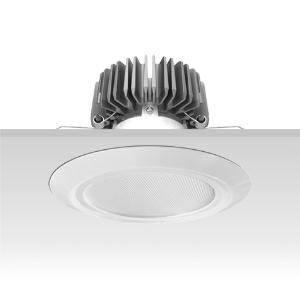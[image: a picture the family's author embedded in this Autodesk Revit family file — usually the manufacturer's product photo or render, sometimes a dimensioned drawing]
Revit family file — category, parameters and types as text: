
# Revit family: 3f_filippi_-_3f_reno_bianco_ampio_3f_filippi_-_30671_a01048_-_3f_reno_200_wh_2000-840_dali_wide___smp_wh_ad90
name_source: partatom
category: Lighting Fixtures
units: mm (PartAtom-declared; Revit-internal decimal feet)

## family parameters
Cut with Voids When Loaded = No
Host = Face
Light Source = No
Part Type = Normal
Room Calculation Point = No
Round Connector Dimension = Use Diameter
Shared = No

## types (1)
- 3F Filippi - 3F Reno Bianco Ampio (1 x LED, 1723 lm, 20 W, 4000 K)
    Apparent Load = 20 VA
    Approval mark = CE
    CIE Flux Codes = 74 92 98 100 100
    Color Rendering = 80
    Color Temperature = 4000 K
    Control Gear = Electronic transformer
    Default Elevation = 1800 mm
    Description = ILLUMINOTECHNICAL
Luminous efficiency 100% (DLOR 100%, ULOR 0%).
Initial luminous flux of the luminaire 1723 lm.
Direct symmetric wide distribution.
Installation Interdistance Transv.D = 1.06 x hu - Long.D = 1.04 x hu.
Average luminance <3000 cd/m² for radial angles >65°.
Tabular UGR (CIE 117 - 4H-8H; S=0.25H; 70/50/20): RUG 21.4 - 21.3.
Beam angle: 70° - 69°.
Luminous efficacy 86 lm/W.
Lifetime (L90/B10): 30000 h. (tq+25°C)
Lifetime (L85/B10): 50000 h. (tq+25°C)
Lifetime (L70/B10): 80000 h. (tq+25°C)
Sudden decreased luminous flux after 50000 hours: 0% (C0).
Photobiological safety in compliance with IEC/TR 62778: RG0 risk exempt, (IEC 62471).
In compliance with IEC/EN 62722-2-1 - IEC/EN 62717 standards.

SOURCE
Compact LED module 2000/840.
Energy efficiency class (UE 2019/2020 - UE 2019/2015): D.
CIE 13.3 Colour rendering index: CRI >80 (R9 <50%).
IES TM-30 Fidelity Index: Rf = 84 Rg = 95.
CCT nominal colour temperature 4000 K.
Colour initial tolerance (MacAdam): SDCM 3.
Zhaga Book 3 compliant.

MECHANICAL
Passive heat dissipator in die-casting aluminium, oversized, for optimum thermal management of the LED module.
Parabolic element with graduated/concentric rings in white polycarbonate.
Transparent external lens with glossy and satin differentiated surfaces, with a cooling and anti-insect system in methacrylate (PMMA).
Fastening spring clips in stainless steel.
Dimensions: diameter 226 mm, height 146 mm. Weight 1.1 kg.
IP44 protection degree for exposed part, IP20 for recessed part.
Mechanical strength to impacts IK05 (0.7 joule).
Glow-wire test resistance 650°C.

ELECTRICAL
Wiring on a separate unit.
Halogen Free DALI-2 DATI (Parts 251, 252, 253), PUSH-DIM, electronic wiring 230V-50/60Hz, power factor 0.90 at full load, THD <25%, constant output current, SELV, class II, 1 driver, 1 DALI addresse.
Power of the luminaire 20 W.
ENEC - CE.
SAFE FLICKER: PstLM=<1 and SVM=<0.4 (IEC TR 61547-1 and IEC TR 63158), to ensure a more comfortable and safe light.
Luminaire compliant with EN 60598-2-22 for power supply from a centralised emergency system CPSS (Central Power Supply System), not incorporated in the luminaire - high risk areas excluded. The default power and flux are 100% in AC and 100% in DC.
Ambient temperature from 0°C to +25°C.
Temperature class T6 max 85°C.
Relative humidity UR: <85%.

INSTALLATION
Pull-up recessed fitting.
False ceiling carving: 200 mm.
All accessories dedicated to this product are available on the Catalog and on our website www.3F-Filippi.com.

ACCESSORIES
A01048 - Anti-glare microprismatic SMP diffuser in methacrylate (PMMA), locked and in line with the trim, in white polycarbonate.

APPLICATIONS
Suitable product for food production plants (HACCP), IFS (Food Version 6), BRC (GSFS Food Version 7).
Environments: architectural, commercial, exhibition areas, transit areas, corridors, shops, display windows, service areas.
In false ceilings with narrow voids.

LIGHT MANAGEMENT
Recommended minimum setting: 10%.
The luminaire, equipped with (DALI-2 DATI) driver, can be controlled manually with 3F Easy Dim technology or automatically/manually with wired or wireless DALI/D2D control systems.
The D2D driver guarantees interoperability with other devices with the same certification by making the following information available:
Device Data (Part 251), Energy Report (Part 252), Diagnosis & Maintenance (Part 253).
In electrical systems without a regulation system (manual or automatic) and DALI bus, a suitable jumper must be made on the DA-DA terminals of the appliance.

WARNING
Luminaire designed for disposal/recycling at end-of-life.
Replaceable (LED only) light source by a professional. Replaceable control gear by a professional.
    Height = 0 mm  [stored 0 ft]
    Lamp = 1 x LED
    Lamp Light Flux = 1723 lm
    Lamp Power = 20 W
    Lamp count = 1
    Length = 226 mm
    Lifetime = 50000 h
    Luminous efficacy = 86 lm/W
    Manufacturer = 3F Filippi
    ModVariant = No
    Model = 3F Filippi - 30671+A01048 - 3F Reno 200 WH 2000-840 DALI WIDE + SMP WH
    Mounting Place = Ceiling
    Mounting Type = Recessed
    Number of Poles = 1
    OnlyDefault = Yes
    Power Factor = 1
    Product Name = 3F Filippi - 3F Reno Bianco Ampio
    Product group = recessed luminaire
    ProductGroupID = 4
    Protection Class = Protection class II
    Protection Degree = IP 20
    RLX_Detail_Level = 1
    RLX_Emergency_Light_Flux = 0 lm
    RLX_Emergency_Type = 0
    RLX_Emergency_Type_DB = No
    RlxData = <blob elided: 96653 chars, md5=e4112703>
    Socket = socket
    Standby Power = 0 W
    System Light Flux = 1723 lm
    System Power = 20 W
    Type Comments = Product without accessories
    Type Image = 3ffilippi_3f_reno_200_wh_vs_smp.jpg
    URL = http://relux.com
    VarID = ---
    Voltage = 0 V
    Weight = 0.00 kg
    Width = 0 mm  [stored 0 ft]

note: [stored X ft] marks values corroborated as IEEE doubles in the binary element streams (Revit-internal decimal feet)

## geometry (parser evidence)
native form markers: Blend x4, Sweep x10
no freeform markers — native parametric forms only
